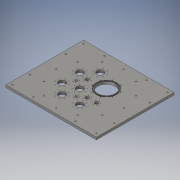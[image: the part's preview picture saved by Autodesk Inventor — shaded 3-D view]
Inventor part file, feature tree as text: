
AUTODESK INVENTOR PART (.ipt)
format: ipt  version: 2018 (Build 220112000, 112)  size: 587,264 bytes
history: native  units: in
note: dims shown in document units (in); Inventor stores cm internally (conversion verified against a paired STEP export)
features: sketch x28, hole x15, extrude x10, pattern_circular x6
ambient origin geometry x8: Origin, YZ Plane, XZ Plane, XY Plane, X Axis, Y Axis, Z Axis, Center Point
bodies: Solid1 (feature_tree)
feature tree (59):
  extrude  "Extrusion1"  Depth=24.0in
  sketch  "Sketch23"  dims[d16=0.267in d17=0.625in d18=0.375in d19=0.25in d20=0.5635in d21=0.833in d22=0.8108in d23=6.5in]
  extrude  "Extrusion2"  Depth=0.75in
  hole  "Hole1"  [1 undecoded]
  sketch  "Sketch58"  dims[d224=0.1in d225=0.0in]
  extrude  "Extrusion22"  Depth=1.0in TaperAngle=0.0deg
  extrude  "Extrusion29"  Depth=3.1496in TaperAngle=360.0deg
  extrude  "Extrusion3"  Depth=6.5in
  hole  "Hole2"  [1 undecoded]
  pattern_circular  "Circular Pattern1"  Count=8 Angle=360.0deg
  extrude  "Extrusion5"  Depth=3.5in
  hole  "Hole20"  [1 undecoded]
  extrude  "Extrusion16"  Depth=1.1811in TaperAngle=180.0deg
  hole  "Hole9"  [1 undecoded]
  pattern_circular  "Circular Pattern6"  Count=6 Angle=360.0deg
  extrude  "Extrusion18"  Depth=6.5in
  hole  "Hole10"  [1 undecoded]
  pattern_circular  "Circular Pattern7"  Count=8 Angle=360.0deg
  hole  "Hole13"  [1 undecoded]
  pattern_circular  "Circular Pattern9"  Count=12 Angle=360.0deg
  extrude  "Extrusion23"  Depth=0.75in
  hole  "Hole19"  [1 undecoded]
  pattern_circular  "Circular Pattern11"  [2 undecoded]
  extrude  "Extrusion27"  Depth=0.75in
  hole  "Hole23"  [1 undecoded]
  hole  "Hole18"  [1 undecoded]
  pattern_circular  "Circular Pattern12"  [2 undecoded]
  hole  "Hole22"  [1 undecoded]
  hole  "Hole24"  [1 undecoded]
  sketch  "Sketch57"  dims[d222=0.7902in d223=2.07in]
  sketch  "Sketch59"  dims[d229=1.625in d230=3.1496in d232=360.0deg]
  sketch  "Sketch62"  dims[d234=0.156in d235=0.38in d236=0.375in d237=0.25in d238=0.5635in d239=0.536in d240=0.8108in d242=0.7874in d243=90.0deg]
  hole  "Hole26"  [1 undecoded]
  hole  "Hole27"  [1 undecoded]
  hole  "Hole28"  [1 undecoded]
  hole  "Hole29"  [1 undecoded]
  sketch  "Sketch1"  dims[d0=28.0in d1=24.0in]
  sketch  "Sketch2"  dims[d2=0.75in d3=0.0in d4=3.6in]
  sketch  "Sketch3"  dims[d5=45.0deg d6=9.35in]
  sketch  "Sketch4"  dims[d7=5.4in d8=1.0in d9=0.0in]
  sketch  "Sketch7"  dims[d10=3.4in d12=3.1496in d14=360.0deg]
  sketch  "Sketch26"  dims[d24=1.4086in d25=2.07in]
  sketch  "Sketch28"  dims[d26=0.1in d27=0.0in]
  sketch  "Sketch30"  dims[d31=1.625in d33=3.1496in d35=360.0deg]
  sketch  "Sketch32"  dims[d37=0.156in d38=0.38in d39=0.375in d40=0.25in d41=0.5635in d42=0.536in d43=0.8108in d44=3.5in]
  sketch  "Sketch37"  dims[d45=2.0958in d46=1.04in]
  sketch  "Sketch38"  dims[d47=0.1in d48=0.0in d134=1.1811in d135=180.0deg]
  sketch  "Sketch39"  dims[d167=21.5in d168=19.125in]
  sketch  "Sketch45"  dims[d185=4.25in]
  sketch  "Sketch49"  dims[d186=180.0deg]
  sketch  "Sketch50"  dims[d187=0.68in]
  sketch  "Sketch51"  dims[d188=0.1in d189=0.0in]
  sketch  "Sketch53"  dims[d193=0.75in]
  sketch  "Sketch54"  dims[d194=180.0deg]
  sketch  "Sketch55"  dims[d195=0.156in d196=0.38in d197=0.375in d198=0.25in d199=0.5635in d200=0.536in d201=0.8108in d202=2.3622in d204=360.0deg]
  sketch  "Sketch56"  dims[d210=0.7874in d211=90.0deg d221=6.5in]
  sketch  "Sketch63"  dims[d277=10.4429in]
  sketch  "Sketch64"  dims[d278=0.354in d279=0.63in d280=0.375in d281=0.25in d282=0.5635in d283=0.831in d284=0.8108in d285=4.7244in d286=360.0deg]
  sketch  "Sketch65"  dims[d288=5.61in d289=5.93in d290=0.104in d291=0.0in d292=7.125in d293=15.125in d294=2.25in d295=135.0deg d296=2.07in d297=0.1in d298=0.0in d321=0.7874in d322=1.3743in d349=5.6in d350=30.0deg d351=1.04in d352=0.1in d353=0.0in d384=6.5in d385=0.0in d388=1.0in d389=45.0deg d390=1.5748in d392=360.0deg d394=0.171in d395=0.432in d396=0.375in d397=0.25in d398=0.5635in d399=0.64in d400=0.8108in d401=1.5748in d402=360.0deg d404=0.5in d405=22.5deg d406=0.5in d407=22.5deg d408=2.0in d409=22.5deg d410=1.625in d411=0.0in d412=3.1496in d414=360.0deg d416=0.156in d417=0.38in d418=0.375in d419=0.25in d420=0.5635in d421=0.536in d422=0.8108in d423=0.9449in d424=0.0in d425=2.3622in d427=360.0deg d429=0.156in d430=0.38in d431=0.375in d432=0.25in d433=0.5635in d434=0.536in d435=0.8108in d448=0.9449in d449=0.1512in d450=2.3622in d452=360.0deg d454=0.156in d455=0.38in d456=0.375in d457=0.25in d458=0.5635in d459=0.536in d460=0.8108in d461=0.9449in d462=30.0deg d463=2.3622in d465=360.0deg d467=0.156in d468=0.38in d469=0.375in d470=0.25in d471=0.5635in d472=0.536in d473=0.8108in d474=1.625in d475=22.5deg d476=3.1496in d478=360.0deg d480=0.156in d481=0.38in d482=0.375in d483=0.25in d484=0.5635in d485=0.536in d486=0.8108in d487=6.068in d488=6.35in d489=0.077in d490=0.0in d491=11.25in d492=14.5in d493=5.1in d494=3.7in d495=7.4in d498=11.0in d499=11.0in d500=10.0in d533=8.5in d534=0.2749in d535=8.5in d536=0.3436in d537=1.5748in d539=360.0deg d541=1.56in d542=45.0deg d543=4.706in d545=4.706in d546=180.0deg d547=0.196in d548=0.4in d549=0.375in d550=0.25in d551=0.5635in d552=0.6in d553=0.8108in d554=0.196in d555=0.4in d556=0.375in d557=0.25in d558=0.5635in d559=0.6in d560=0.8108in d561=1.56in d562=45.0deg d563=7.75in d564=0.8933in d565=7.75in d566=0.962in d567=0.196in d568=0.4in d569=0.375in d570=0.25in d571=0.5635in d572=0.6in d573=0.8108in d574=6.9473in d575=13.0in d576=0.7874in d578=360.0deg d580=26.0in d581=22.0in d582=6.5in d583=0.0in d584=0.397in d585=0.75in d586=0.762in d587=0.25in d588=0.5635in d589=1.0in d590=0.8108in d591=5.5in d592=5.5in]
note: 19 required parameter values undecoded (feature->parameter linkage not recoverable at this tier; creation-order binding heuristic only, values carry confidence <= 0.55)
